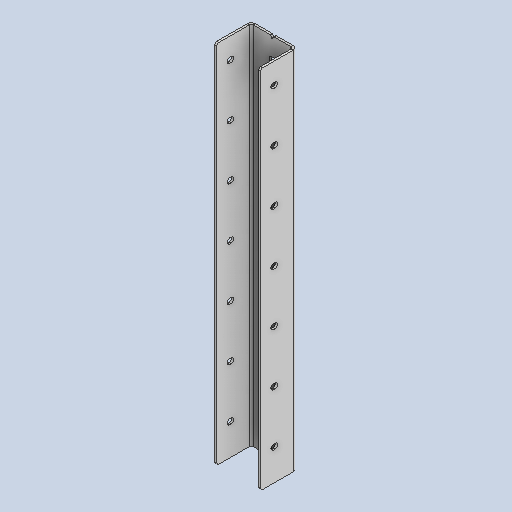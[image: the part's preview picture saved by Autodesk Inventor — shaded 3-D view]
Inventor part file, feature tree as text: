
AUTODESK INVENTOR PART (.ipt)
format: ipt  version: 2025 (Build 290162010, 162A)  size: 352,768 bytes
history: native  units: mm
features: sheet_metal_op x4, extrude x3, other x3, fillet x2, pattern_linear x1, mirror x1, sketch x1, projected_geometry x1
ambient origin geometry x8: Origin, YZ Plane, XZ Plane, XY Plane, X Axis, Y Axis, Z Axis, Center Point
bodies: Solid1 (feature_tree)
feature tree (16):
  sheet_metal_op  "Face1"
  sheet_metal_op  "Flange1"
  extrude  "Extrusion1"  Depth=350.0mm
  extrude  "Extrusion2"  Depth=2.0mm
  pattern_linear  "Rectangular Pattern2"  Spacing1=2.0mm  [1 undecoded]
  fillet  "Fillet1"  Radius=1.0mm
  extrude  "Extrusion3"  Depth=4.0mm
  fillet  "Fillet2"  Radius=2.0mm
  mirror  "Mirror1"
  other  "Plate1"
  sketch  "Sketch2"  dims[d0=40.0mm d1=350.0mm d2=2.0mm d3=2.0mm d4=1.0mm d5=4.0mm d6=2.0mm d7=35.0mm d8=90.0deg d9=2.0mm d10=8.0mm d11=2.0mm d12=2.0mm d13=5.0mm d14=13.0mm d15=30.0mm d16=0.0mm d17=0.0mm d21=5.0mm d22=30.0mm d23=0.0mm d24=0.0mm d25=70.0mm d27=50.0mm d28=1.0mm d29=1.5mm d30=2.0mm d31=3.0mm d32=3.0mm d33=0.0mm d34=0.0mm d35=0.5mm]
  other  "Plate2"
  sheet_metal_op  "Bend1"
  sheet_metal_op  "Corner1"
  projected_geometry  "Projected Loop1"
  other  "Definition1"
note: 1 required parameter value undecoded (feature->parameter linkage not recoverable at this tier; creation-order binding heuristic only, values carry confidence <= 0.55)
